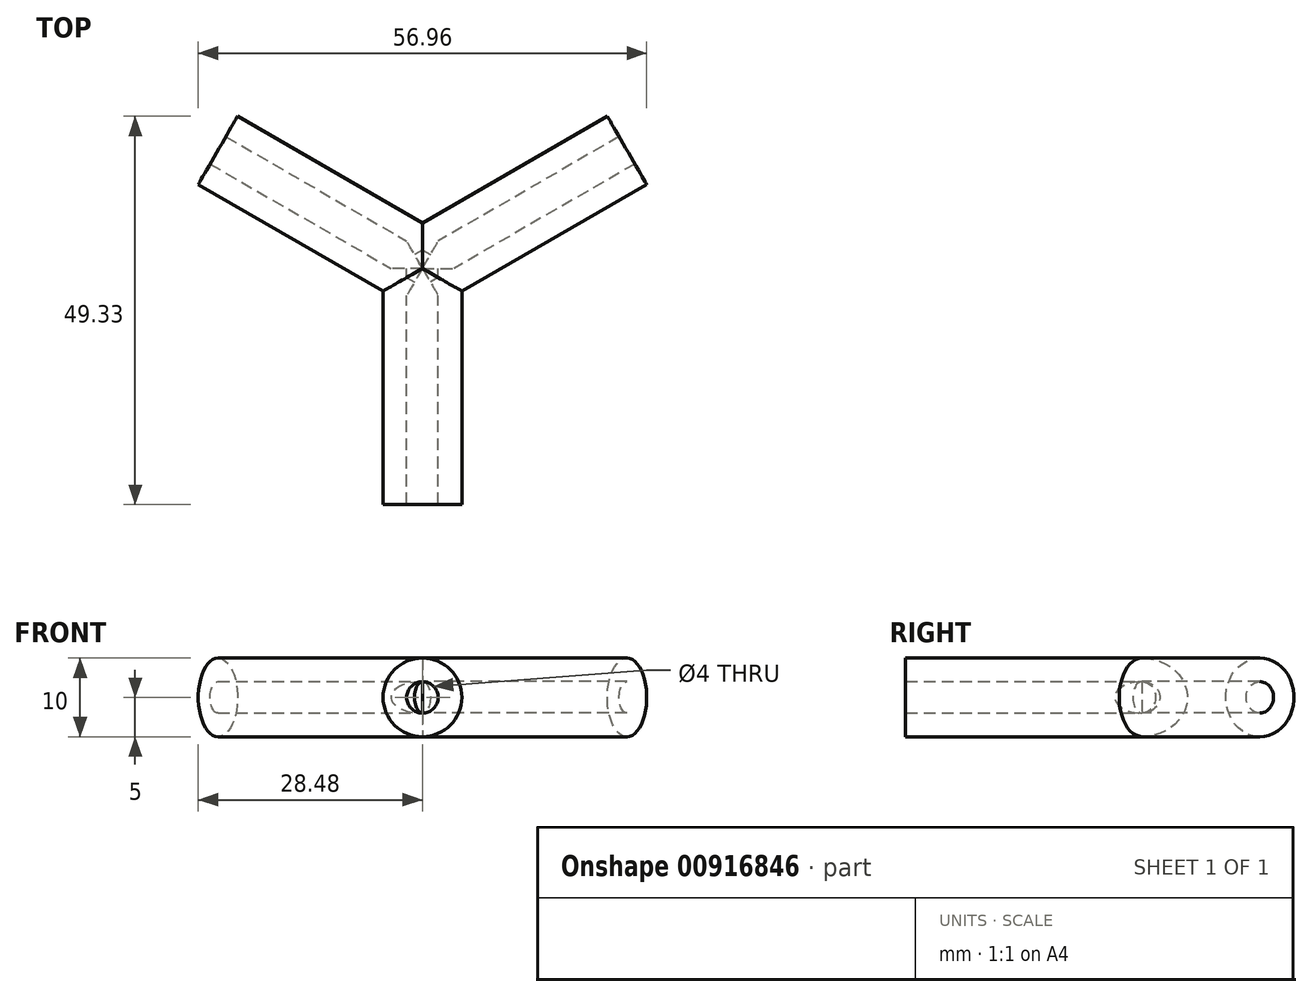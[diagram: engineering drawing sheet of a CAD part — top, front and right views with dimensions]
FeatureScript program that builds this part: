
annotation { "Feature Type Name" : "Feature", "Feature Type Description" : "" }
export const myFeature = defineFeature(function(context is Context, id is Id, definition is map)
    precondition{}
    {
        {
            var Q0;
            Q0=qCreatedBy(makeId("Front.planeOp"),FACE);
            var sketch = newSketch(context, id + "F0", { "sketchPlane" : qUnion([Q0])});
            skCircle(sketch, "E0", {"center": v(0, 0) * mm, "radius": 5 * mm});
            skCircle(sketch, "E1", {"center": v(0, 0) * mm, "radius": 2 * mm});
            skSolve(sketch);
        }
        {
            var Q0;
            Q0=qSketchRegion(id+"F0",true);
            extrude(context, id + "F1", {"entities" : qUnion([Q0]), "depth" : 30 * mm, "offsetDistance" : 25 * mm});
        }
        {
            var Q0;
            Q0=qCreatedBy(makeId("Front.planeOp"),FACE);
            var sketch = newSketch(context, id + "F2", { "sketchPlane" : qUnion([Q0])});
            skLineSegment(sketch, "E2", {"start": v(0, 0) * mm, "end": v(0, 70.28) * mm});
            skSolve(sketch);
        }
        {
            var Q0;
            Q0=makeQuery(id+"F1.opExtrude","SWEPT_BODY",BODY,{"disambiguationData":[OSD([sQuery(id+"F0.wireOp",EDGE,"E0")])]});
            var Q1;
            Q1=sQuery(id+"F2.wireOp",EDGE,"E2");
            circularPattern(context, id + "F3", {"operationType" : NewBodyOperationType.ADD, "entities" : qUnion([Q0]), "axis" : qUnion([Q1]), "angle" : 360 * degree, "instanceCount" : 3, "equalSpace" : true});
        }
    });
